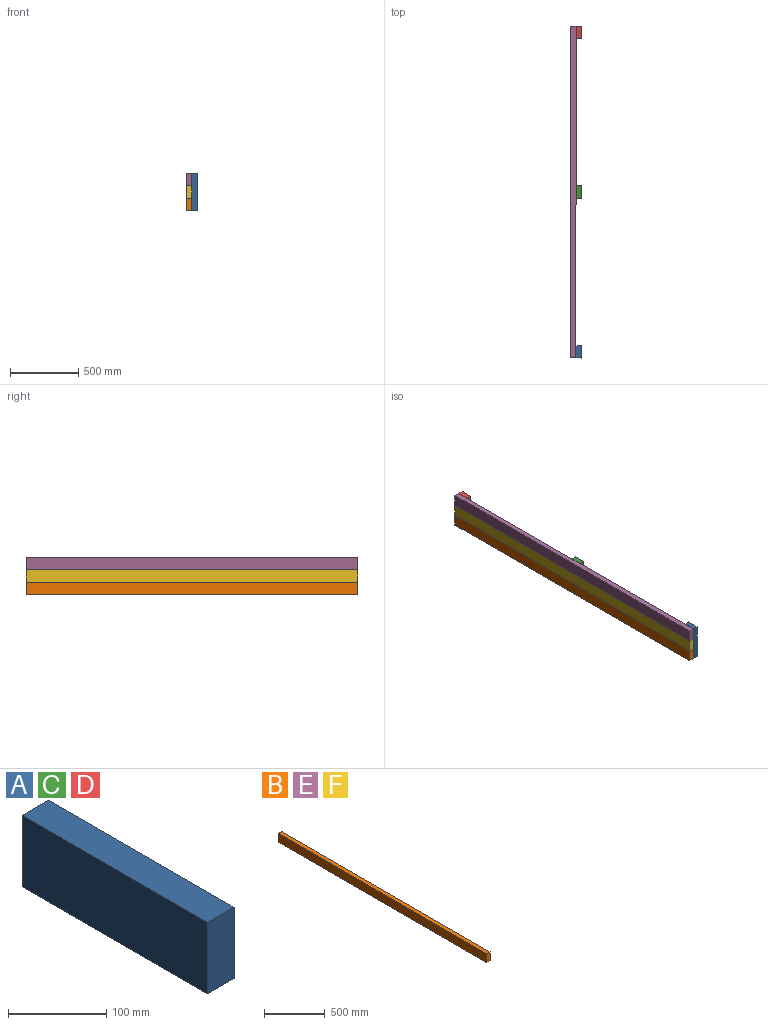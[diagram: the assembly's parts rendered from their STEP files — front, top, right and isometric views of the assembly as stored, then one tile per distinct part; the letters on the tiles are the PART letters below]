
ASSEMBLY  parts=6 mates=5
PART A: 6 faces, bbox 38.1x266.7x88.9 mm
  f0: plane 266.7x38.1mm, normal (0,0,1), area 10161.3mm2, adj f1,f3,f4,f5
  f1: plane 266.7x88.9mm, normal (-1,0,0), area 23709.6mm2, adj f0,f2,f4,f5
  f2: plane 266.7x38.1mm, normal (0,0,-1), area 10161.3mm2, adj f1,f3,f4,f5
  f3: plane 266.7x88.9mm, normal (1,0,0), area 23709.6mm2, adj f0,f2,f4,f5
  f4: plane 88.9x38.1mm, normal (0,-1,0), area 3387.1mm2, adj f0,f1,f2,f3
  f5: plane 88.9x38.1mm, normal (0,1,0), area 3387.1mm2, adj f0,f1,f2,f3
PART B: 6 faces, bbox 38.1x2438.4x88.9 mm
  f0: plane 2438.4x38.1mm, normal (0,0,1), area 92903mm2, adj f1,f3,f4,f5
  f1: plane 2438.4x88.9mm, normal (-1,0,0), area 216773.8mm2, adj f0,f2,f4,f5
  f2: plane 2438.4x38.1mm, normal (0,0,-1), area 92903mm2, adj f1,f3,f4,f5
  f3: plane 2438.4x88.9mm, normal (1,0,0), area 216773.8mm2, adj f0,f2,f4,f5
  f4: plane 88.9x38.1mm, normal (0,-1,0), area 3387.1mm2, adj f0,f1,f2,f3
  f5: plane 88.9x38.1mm, normal (0,1,0), area 3387.1mm2, adj f0,f1,f2,f3
PART C: same geometry as A
PART D: same geometry as A
PART E: same geometry as B
PART F: same geometry as B
PLACE A rot(axis=(0,-0.71,0.71),180deg) t=(-396.88,-983.07,-70.54)mm
PLACE B t=(-434.98,191.68,-159.44)mm
PLACE C rot(axis=(0,0.71,0.71),180deg) t=(-396.88,191.68,-70.54)mm
PLACE D rot(axis=(0,-0.71,0.71),180deg) t=(-396.88,1366.43,-70.54)mm
PLACE E rot(axis=(-1,0,0),180deg) t=(-434.98,191.68,18.36)mm
PLACE F t=(-434.98,191.68,-70.54)mm
MATE fastened D.f3 <-> F.f3  axis (-1,0,0) through (-415.93,1410.88,-70.54)mm
MATE fastened F.f0 <-> E.f0  axis (0,0,1) through (-434.98,191.68,-26.09)mm
MATE fastened A.f3 <-> F.f3  axis (-1,0,0) through (-415.93,-1027.52,-70.54)mm
MATE fastened F.f2 <-> B.f0  axis (0,0,-1) through (-434.98,191.68,-114.99)mm
MATE fastened C.f3 <-> F.f3  axis (-1,0,0) through (-415.93,191.68,-70.54)mm
